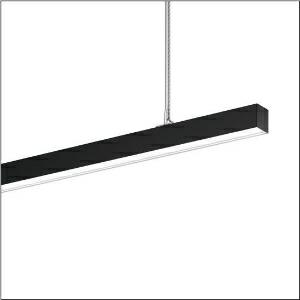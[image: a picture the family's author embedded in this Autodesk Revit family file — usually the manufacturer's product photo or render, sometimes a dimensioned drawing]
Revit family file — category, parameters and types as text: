
# Revit family: silica_r__21_51mx30da44bb_2b52
name_source: partatom
category: Lighting Fixtures
units: mm (PartAtom-declared; Revit-internal decimal feet)

## family parameters
Cut with Voids When Loaded = No
Host = Face
Light Source = No
Part Type = Normal
Room Calculation Point = No
Round Connector Dimension = Use Diameter
Shared = No

## types (1)
- --- (1 x LED, 4210 lm, 26 W, 4000K)
    Apparent Load = 26 VA
    CIE Flux Codes = 47 79 96 57 100
    Color Rendering = 80
    Color Temperature = 4000K
    Default Elevation = 1800 mm
    Description = Silica® 21, office luminaire, primary optical cover: cover, of PMMA, opal, light emission: direct/indirect distribution, primary light characteristic: symmetric, installation type: suspended mounting, LED, rated luminous flux: 4.210lm, luminous efficacy: 162lm/W, light colour: 840, colour temperature: 4000K, control gear: DALI 2, with terminal, 3+2-pole, max. 2.5mm², mains connection: 220..240V, AC, 50/60Hz, rated input power: 26W, luminaire housing, of aluminium, matt jet black (RAL 9005), length: 1.204mm, width: 53mm, height: 53mm, protection rating (complete): IP20, insulation class (complete): insulation class I (protective earthing), certification: CE, permissible operating ambient temperature: 0..+35°C, standard: EN 50419, packaging unit: 1 piece
    Height = 53 mm
    Lamp = 1 x LED
    Lamp Light Flux = 4210 lm
    Lamp Power = 26 W
    Lamp count = 1
    Length = 1204 mm
    Luminous efficacy = 162 lm/W
    Manufacturer = Siteco
    ModVariant = No
    Model = 51MX30DA44BB
    Mounting Place = Ceiling
    Mounting Type = Pendant
    Number of Poles = 1
    OnlyDefault = Yes
    Power Factor = 1
    Product Name = Silica® 21
    Product group = office luminaire | ceiling pendant
    ProductGroupID = 903
    Protection Class = Protection class I
    Protection Degree = IP 20
    RLX_Detail_Level = 1
    RLX_Emergency_Light_Flux = 0 lm
    RLX_Emergency_Type = 0
    RLX_Emergency_Type_DB = No
    RlxData = <blob elided: 25873 chars, md5=0957014e>
    Socket = socket
    Standby Power = 0 W
    System Light Flux = 4210 lm
    System Power = 26 W
    Type Comments = factory setting: luminous flux: 100 % | dim-lin: 254 | 218 mA
    Type Image = l_1335856.jpg
    URL = http://relux.com
    VarID = @adj_138871
    Voltage = 0 V
    Weight = 0.00 kg
    Width = 53 mm

## geometry (parser evidence)
native form markers: Blend x4, Sweep x11
no freeform markers — native parametric forms only
